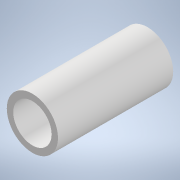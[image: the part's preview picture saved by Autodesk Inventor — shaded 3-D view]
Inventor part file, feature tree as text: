
AUTODESK INVENTOR PART (.ipt)
format: ipt  version: 2022 (Build 260153000, 153)  size: 95,744 bytes
history: native  units: mm
features: extrude x1, sketch x1
ambient origin geometry x8: Origin, YZ Plane, XZ Plane, XY Plane, X Axis, Y Axis, Z Axis, Center Point
bodies: Solid1 (feature_tree)
feature tree (2):
  extrude  "Extrusion1"  Depth=18.0mm
  sketch  "Sketch1"  dims[d0=6.0mm d1=8.0mm d2=18.0mm d3=0.0mm]
